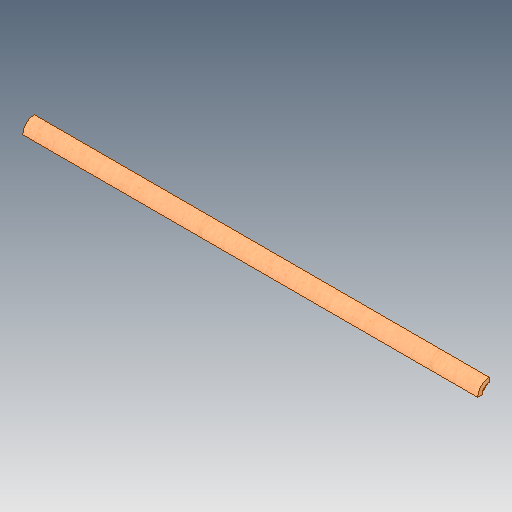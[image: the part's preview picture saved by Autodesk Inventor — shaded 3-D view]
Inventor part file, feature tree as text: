
AUTODESK INVENTOR PART (.ipt)
format: ipt  version: 2018.2 (Build 222227000, 227)  size: 120,320 bytes
history: native  units: mm
features: sketch x2, extrude x1, chamfer x1, fillet x1, revolve x1, mirror x1, projected_geometry x1
ambient origin geometry x8: Origin, YZ Plane, XZ Plane, XY Plane, X Axis, Y Axis, Z Axis, Center Point
bodies: Solid1 (feature_tree)
feature tree (8):
  extrude  "Extrusion1"  Depth=12.7mm
  chamfer  "Chamfer1"  [1 undecoded]
  fillet  "Fillet1"  Radius=6.35mm
  revolve  "Revolution1"  Angle=45.0deg
  mirror  "Mirror1"
  sketch  "Sketch1"  dims[d0=12.7mm d1=12.7mm]
  sketch  "Sketch2"  dims[d2=500.0mm d3=0.0mm d4=6.35mm d5=2.0mm d6=45.0deg d7=12.7mm d8=3.175mm d9=90.0deg]
  projected_geometry  "Projected Loop1"
note: 1 required parameter value undecoded (feature->parameter linkage not recoverable at this tier; creation-order binding heuristic only, values carry confidence <= 0.55)
